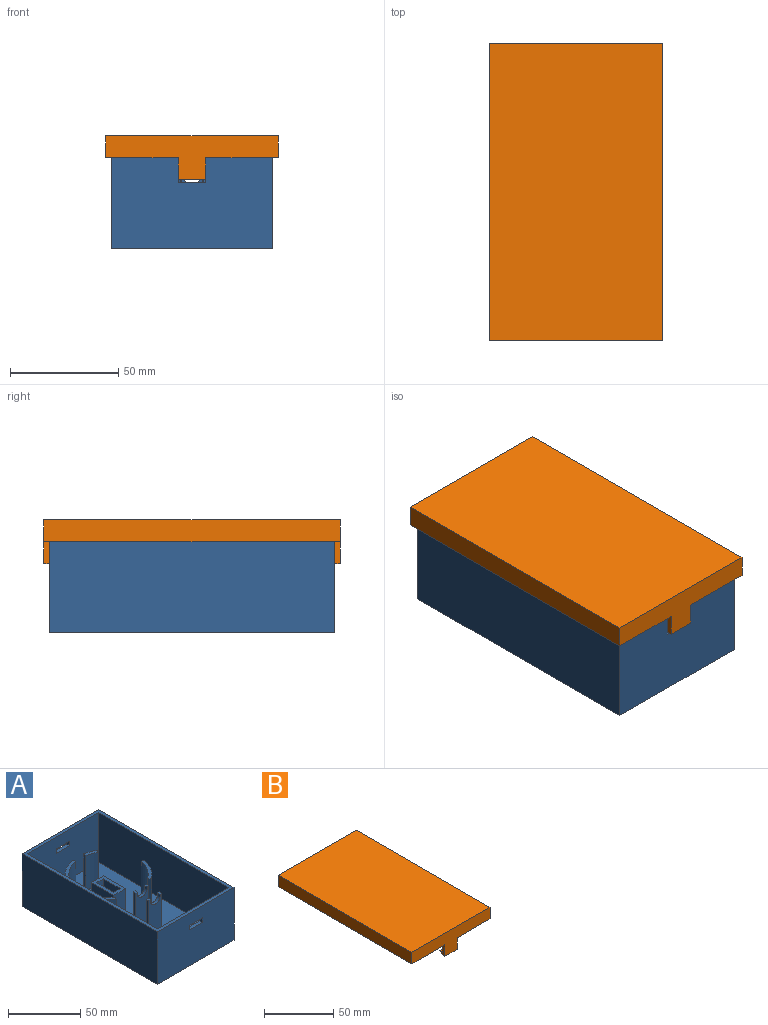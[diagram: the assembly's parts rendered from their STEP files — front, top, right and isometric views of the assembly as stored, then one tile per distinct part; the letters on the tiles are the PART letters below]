
ASSEMBLY  parts=2 mates=1
PART A: 63 faces, bbox 74.9x132.1x44.5 mm
  f0: plane 69.85x41.91mm, normal (0,-1,0), area 2878.5mm2, adj f10,f49,f50,f53,f59,f60,f61,f62
  f1: plane 74.93x44.45mm, normal (0,1,0), area 3281.8mm2, adj f51,f52,f53,f54,f59,f60,f61,f62
  f2: plane 69.85x41.91mm, normal (0,1,0), area 2878.5mm2, adj f10,f49,f50,f53,f55,f56,f57,f58
  f3: plane 74.93x44.45mm, normal (0,-1,0), area 3281.8mm2, adj f51,f52,f53,f54,f55,f56,f57,f58
  f4: plane 2.54x1.76mm, normal (0,0,1), area 4.5mm2, adj f32,f33,f34,f48
  f5: plane 2.54x1.76mm, normal (0,0,1), area 4.5mm2, adj f36,f37,f38,f47
  f6: plane 21.59x19.81mm, normal (1,0,0), area 427.7mm2, adj f7,f9,f10,f39
  f7: plane 19.81x11.43mm, normal (0,1,0), area 226.5mm2, adj f6,f8,f10,f39
  f8: plane 21.59x19.81mm, normal (-1,0,0), area 427.7mm2, adj f7,f9,f10,f39
  f9: plane 19.81x11.43mm, normal (0,-1,0), area 226.5mm2, adj f6,f8,f10,f39
  f10: plane 127x69.85mm, normal (0,0,1), area 8362.4mm2, adj f0,f2,f6,f7,f8,f9,f11,f12
  f11: plane 29.21x2.08mm, normal (0.82,-0.57,0), area 74.2mm2, adj f10,f12,f14,f15
  f12: cylinder r=27.43mm len=29.21mm, axis (0,0,-1), area 629.3mm2, adj f10,f11,f13,f15
  f13: plane 29.21x2.5mm, normal (-0.17,0.98,0), area 74.2mm2, adj f10,f12,f14,f15
  f14: cylinder r=29.97mm len=29.21mm, axis (0,0,-1), area 687.6mm2, adj f10,f11,f13,f15
  f15: plane 19.79x13.78mm, normal (0,0,1), area 57.3mm2, adj f11,f12,f13,f14
  f16: plane 29.21x2.5mm, normal (0.98,0.17,0), area 74.2mm2, adj f10,f17,f19,f20
  f17: cylinder r=29.97mm len=29.21mm, axis (0,0,-1), area 687.6mm2, adj f10,f16,f18,f20
  f18: plane 29.21x2.08mm, normal (-0.57,-0.82,0), area 74.2mm2, adj f10,f17,f19,f20
  f19: cylinder r=27.43mm len=29.21mm, axis (0,0,-1), area 629.3mm2, adj f10,f16,f18,f20
  f20: plane 19.79x13.78mm, normal (0,0,1), area 57.3mm2, adj f16,f17,f18,f19
  f21: cylinder r=27.43mm len=29.21mm, axis (0,0,-1), area 279.7mm2, adj f10,f22,f24,f25
  f22: plane 29.21x2.2mm, normal (0.87,-0.5,0), area 74.2mm2, adj f10,f21,f23,f25
  f23: cylinder r=29.97mm len=29.21mm, axis (0,0,-1), area 305.6mm2, adj f10,f22,f24,f25
  f24: plane 29.21x2.5mm, normal (-0.98,0.17,0), area 74.2mm2, adj f10,f21,f23,f25
  f25: plane 10.22x5.76mm, normal (0,0,1), area 25.4mm2, adj f21,f22,f23,f24
  f26: plane 29.21x2.08mm, normal (-0.82,-0.57,0), area 74.2mm2, adj f10,f27,f29,f30
  f27: cylinder r=29.97mm len=29.21mm, axis (0,0,-1), area 687.6mm2, adj f10,f26,f28,f30
  f28: plane 29.21x2.5mm, normal (0.17,0.98,0), area 74.2mm2, adj f10,f27,f29,f30
  f29: cylinder r=27.43mm len=29.21mm, axis (0,0,-1), area 629.3mm2, adj f10,f26,f28,f30
  f30: plane 19.79x13.78mm, normal (0,0,1), area 57.3mm2, adj f26,f27,f28,f29
  f31: plane 33.02x2.54mm, normal (1,0,0), area 83.9mm2, adj f10,f32,f34,f45
  f32: plane 33.02x12.7mm, normal (0,1,0), area 371.8mm2, adj f4,f10,f31,f33,f45,f48
  f33: plane 33.02x2.54mm, normal (-1,0,0), area 83.9mm2, adj f4,f10,f32,f34
  f34: plane 33.02x12.7mm, normal (0,-1,0), area 371.8mm2, adj f4,f10,f31,f33,f45,f48
  f35: plane 33.02x2.54mm, normal (1,0,0), area 83.9mm2, adj f10,f36,f38,f46
  f36: plane 33.02x12.7mm, normal (0,1,0), area 371.8mm2, adj f5,f10,f35,f37,f46,f47
  f37: plane 33.02x2.54mm, normal (-1,0,0), area 83.9mm2, adj f5,f10,f36,f38
  f38: plane 33.02x12.7mm, normal (0,-1,0), area 371.8mm2, adj f5,f10,f35,f37,f46,f47
  f39: plane 21.59x11.43mm, normal (0,0,1), area 141.9mm2, adj f6,f7,f8,f9,f41,f42,f43,f44
  f40: plane 16.51x6.35mm, normal (0,0,1), area 104.8mm2, adj f41,f42,f43,f44
  f41: plane 19.81x16.51mm, normal (1,0,0), area 327.1mm2, adj f39,f40,f42,f44
  f42: plane 19.81x6.35mm, normal (0,1,0), area 125.8mm2, adj f39,f40,f41,f43
  f43: plane 19.81x16.51mm, normal (-1,0,0), area 327.1mm2, adj f39,f40,f42,f44
  f44: plane 19.81x6.35mm, normal (0,-1,0), area 125.8mm2, adj f39,f40,f41,f43
  f45: plane 2.54x1.76mm, normal (0,0,1), area 4.5mm2, adj f31,f32,f34,f48
  f46: plane 2.54x1.76mm, normal (0,0,1), area 4.5mm2, adj f35,f36,f38,f47
  f47: cylinder r=4.76mm len=9.53mm, axis (0,-1,0), area 44.5mm2, adj f5,f36,f38,f46
  f48: cylinder r=4.76mm len=9.53mm, axis (0,-1,0), area 44.5mm2, adj f4,f32,f34,f45
  f49: plane 127x41.91mm, normal (-1,0,0), area 5322.6mm2, adj f0,f2,f10,f53
  f50: plane 127x41.91mm, normal (1,0,0), area 5322.6mm2, adj f0,f2,f10,f53
  f51: plane 132.08x44.45mm, normal (1,0,0), area 5871mm2, adj f1,f3,f53,f54
  f52: plane 132.08x44.45mm, normal (-1,0,0), area 5871mm2, adj f1,f3,f53,f54
  f53: plane 132.08x74.93mm, normal (0,0,1), area 1025.8mm2, adj f0,f1,f2,f3,f49,f50,f51,f52
  f54: plane 132.08x74.93mm, normal (0,0,-1), area 9896.8mm2, adj f1,f3,f51,f52
  f55: plane 3.81x2.54mm, normal (-1,0,0), area 9.7mm2, adj f2,f3,f56,f58
  f56: plane 12.83x2.54mm, normal (0,0,-1), area 32.6mm2, adj f2,f3,f55,f57
  f57: plane 3.81x2.54mm, normal (1,0,0), area 9.7mm2, adj f2,f3,f56,f58
  f58: plane 12.83x2.54mm, normal (0,0,1), area 32.6mm2, adj f2,f3,f55,f57
  f59: plane 12.83x2.54mm, normal (0,0,-1), area 32.6mm2, adj f0,f1,f60,f62
  f60: plane 3.81x2.54mm, normal (-1,0,0), area 9.7mm2, adj f0,f1,f59,f61
  f61: plane 12.83x2.54mm, normal (0,0,1), area 32.6mm2, adj f0,f1,f60,f62
  f62: plane 3.81x2.54mm, normal (1,0,0), area 9.7mm2, adj f0,f1,f59,f61
PART B: 27 faces, bbox 80x137.2x20.3 mm
  f0: plane 137.16x33.66mm, normal (0,0,-1), area 506.5mm2, adj f3,f4,f6,f7,f8,f9,f14,f19
  f1: plane 137.16x33.66mm, normal (0,0,-1), area 506.5mm2, adj f4,f5,f6,f7,f9,f10,f15,f20
  f2: plane 137.16x80.01mm, normal (0,0,1), area 10974.2mm2, adj f7,f8,f9,f10
  f3: plane 132.08x2.54mm, normal (-1,0,0), area 335.5mm2, adj f0,f4,f6,f25
  f4: plane 74.93x10.16mm, normal (0,-1,0), area 287.1mm2, adj f0,f1,f3,f5,f16,f19,f20,f25
  f5: plane 132.08x2.54mm, normal (1,0,0), area 335.5mm2, adj f1,f4,f6,f25
  f6: plane 74.93x10.16mm, normal (0,1,0), area 287.1mm2, adj f0,f1,f3,f5,f13,f14,f15,f25
  f7: plane 80.01x20.32mm, normal (0,1,0), area 941.9mm2, adj f0,f1,f2,f8,f10,f18,f19,f20
  f8: plane 137.16x10.16mm, normal (1,0,0), area 1393.5mm2, adj f0,f2,f7,f9
  f9: plane 80.01x20.32mm, normal (0,-1,0), area 941.9mm2, adj f0,f1,f2,f8,f10,f11,f14,f15
  f10: plane 137.16x10.16mm, normal (-1,0,0), area 1393.5mm2, adj f1,f2,f7,f9
  f11: plane 12.7x2.54mm, normal (0,0,-1), area 32.3mm2, adj f9,f12,f14,f15
  f12: plane 12.7x2.54mm, normal (0,0.71,-0.71), area 45.6mm2, adj f11,f13,f14,f15
  f13: plane 12.7x2.54mm, normal (0,0,1), area 32.3mm2, adj f6,f12,f14,f15
  f14: plane 10.16x5.08mm, normal (1,0,0), area 29mm2, adj f0,f6,f9,f11,f12,f13
  f15: plane 10.16x5.08mm, normal (-1,0,0), area 29mm2, adj f1,f6,f9,f11,f12,f13
  f16: plane 12.7x2.54mm, normal (0,0,1), area 32.3mm2, adj f4,f17,f19,f20
  f17: plane 12.7x2.54mm, normal (0,-0.71,-0.71), area 45.6mm2, adj f16,f18,f19,f20
  f18: plane 12.7x2.54mm, normal (0,0,-1), area 32.3mm2, adj f7,f17,f19,f20
  f19: plane 10.16x5.08mm, normal (1,0,0), area 29mm2, adj f0,f4,f7,f16,f17,f18
  f20: plane 10.16x5.08mm, normal (-1,0,0), area 29mm2, adj f1,f4,f7,f16,f17,f18
  f21: plane 127x5.08mm, normal (1,0,0), area 645.2mm2, adj f22,f24,f25,f26
  f22: plane 69.85x5.08mm, normal (0,1,0), area 354.8mm2, adj f21,f23,f25,f26
  f23: plane 127x5.08mm, normal (-1,0,0), area 645.2mm2, adj f22,f24,f25,f26
  f24: plane 69.85x5.08mm, normal (0,-1,0), area 354.8mm2, adj f21,f23,f25,f26
  f25: plane 132.08x74.93mm, normal (0,0,-1), area 1025.8mm2, adj f3,f4,f5,f6,f21,f22,f23,f24
  f26: plane 127x69.85mm, normal (0,0,-1), area 8870.9mm2, adj f21,f22,f23,f24
PLACE A rot(axis=(0,0,-1),180deg) t=(-37.47,-17.4,-25.49)mm
PLACE B t=(-37.47,1.65,21.5)mm
MATE planar A.f53 <-> B.f25  axis (0,0,1) through (0,67.69,16.42)mm
